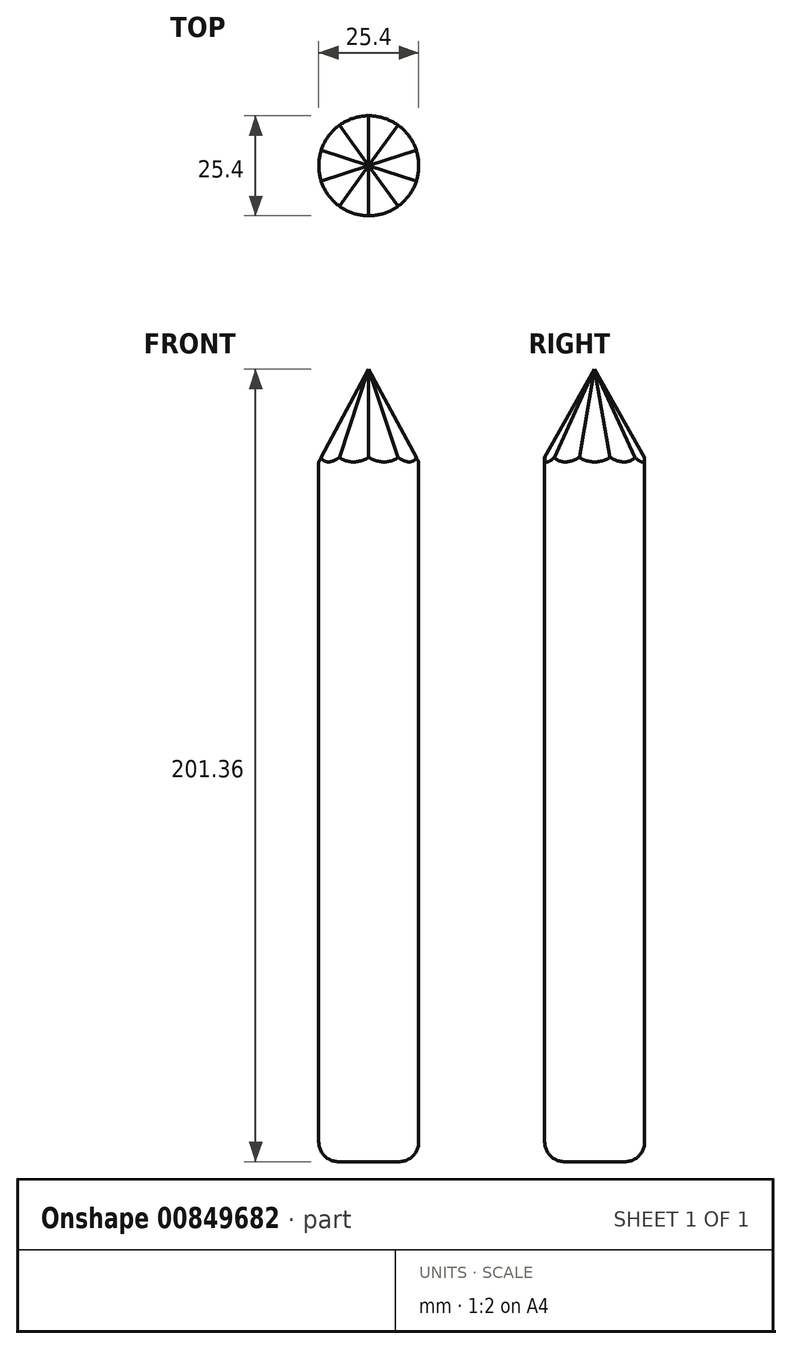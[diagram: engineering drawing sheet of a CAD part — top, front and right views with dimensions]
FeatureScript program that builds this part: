
annotation { "Feature Type Name" : "Feature", "Feature Type Description" : "" }
export const myFeature = defineFeature(function(context is Context, id is Id, definition is map)
    precondition{}
    {
        {
            var Q0;
            Q0=qCreatedBy(makeId("Top.planeOp"),FACE);
            var sketch = newSketch(context, id + "F0", { "sketchPlane" : qUnion([Q0])});
            skCircle(sketch, "E0.cCircle", {"center": v(0, 0) * mm, "radius": 12.7 * mm, "construction": true});
            skLineSegment(sketch, "E0.0", {"start": v(-12.7, -4.13) * mm, "end": v(-12.7, 4.13) * mm});
            skLineSegment(sketch, "E0.1", {"start": v(-12.7, 4.13) * mm, "end": v(-7.85, 10.8) * mm});
            skLineSegment(sketch, "E0.2", {"start": v(-7.85, 10.8) * mm, "end": v(0, 13.35) * mm});
            skLineSegment(sketch, "E0.3", {"start": v(0, 13.35) * mm, "end": v(7.85, 10.8) * mm});
            skLineSegment(sketch, "E0.4", {"start": v(7.85, 10.8) * mm, "end": v(12.7, 4.13) * mm});
            skLineSegment(sketch, "E0.5", {"start": v(12.7, 4.13) * mm, "end": v(12.7, -4.13) * mm});
            skLineSegment(sketch, "E0.6", {"start": v(12.7, -4.13) * mm, "end": v(7.85, -10.8) * mm});
            skLineSegment(sketch, "E0.7", {"start": v(7.85, -10.8) * mm, "end": v(0, -13.35) * mm});
            skLineSegment(sketch, "E0.8", {"start": v(0, -13.35) * mm, "end": v(-7.85, -10.8) * mm});
            skLineSegment(sketch, "E0.9", {"start": v(-7.85, -10.8) * mm, "end": v(-12.7, -4.13) * mm});
            skPoint(sketch, "E0.0.midPoint", {"position": v(-12.7, 0) * mm});
            skSolve(sketch);
        }
        {
            var Q0;
            Q0=qSketchRegion(id+"F0",true);
            extrude(context, id + "F1", {"entities" : qUnion([Q0]), "depth" : 177.8 * mm, "offsetDistance" : 25.4 * mm});
        }
        {
            var Q0;
            Q0=qCreatedBy(makeId("Front.planeOp"),FACE);
            var sketch = newSketch(context, id + "F2", { "sketchPlane" : qUnion([Q0])});
            skPoint(sketch, "E1", {"position": v(0, 201.36) * mm});
            skSolve(sketch);
        }
        {
            var Q1;
            Q1=makeQuery(id+"F1.opExtrude","CAP_FACE",FACE,{"disambiguationData":[OSD([sQuery(id+"F0.wireOp",EDGE,"E0.0"),sQuery(id+"F0.wireOp",EDGE,"E0.1"),sQuery(id+"F0.wireOp",EDGE,"E0.2"),sQuery(id+"F0.wireOp",EDGE,"E0.3"),sQuery(id+"F0.wireOp",EDGE,"E0.4"),sQuery(id+"F0.wireOp",EDGE,"E0.5"),sQuery(id+"F0.wireOp",EDGE,"E0.6"),sQuery(id+"F0.wireOp",EDGE,"E0.7"),sQuery(id+"F0.wireOp",EDGE,"E0.8"),sQuery(id+"F0.wireOp",EDGE,"E0.9")])],"isStart":false});
            var Q2;
            Q2=sQuery(id+"F2.wireOp",VERTEX,"E1");
            loft(context, id + "F3", {"operationType" : NewBodyOperationType.ADD, "sheetProfilesArray" : [{ "sheetProfileEntities" : qUnion([Q1]) }, { "sheetProfileEntities" : qUnion([Q2]) }]});
        }
        {
            var Q0;
            Q0=makeQuery(id+"F1.opExtrude","SWEPT_EDGE",EDGE,{"disambiguationData":[OSD([sQuery(id+"F0.wireOp",EDGE,"E0.7"),sQuery(id+"F0.wireOp",EDGE,"E0.8")])]});
            var Q1;
            Q1=makeQuery(id+"F1.opExtrude","SWEPT_EDGE",EDGE,{"disambiguationData":[OSD([sQuery(id+"F0.wireOp",EDGE,"E0.8"),sQuery(id+"F0.wireOp",EDGE,"E0.9")])]});
            var Q2;
            Q2=makeQuery(id+"F1.opExtrude","SWEPT_EDGE",EDGE,{"disambiguationData":[OSD([sQuery(id+"F0.wireOp",EDGE,"E0.0"),sQuery(id+"F0.wireOp",EDGE,"E0.9")])]});
            var Q3;
            Q3=makeQuery(id+"F1.opExtrude","SWEPT_EDGE",EDGE,{"disambiguationData":[OSD([sQuery(id+"F0.wireOp",EDGE,"E0.0"),sQuery(id+"F0.wireOp",EDGE,"E0.1")])]});
            var Q4;
            Q4=makeQuery(id+"F1.opExtrude","SWEPT_EDGE",EDGE,{"disambiguationData":[OSD([sQuery(id+"F0.wireOp",EDGE,"E0.1"),sQuery(id+"F0.wireOp",EDGE,"E0.2")])]});
            var Q5;
            Q5=makeQuery(id+"F1.opExtrude","SWEPT_EDGE",EDGE,{"disambiguationData":[OSD([sQuery(id+"F0.wireOp",EDGE,"E0.2"),sQuery(id+"F0.wireOp",EDGE,"E0.3")])]});
            var Q6;
            Q6=makeQuery(id+"F1.opExtrude","SWEPT_EDGE",EDGE,{"disambiguationData":[OSD([sQuery(id+"F0.wireOp",EDGE,"E0.3"),sQuery(id+"F0.wireOp",EDGE,"E0.4")])]});
            var Q7;
            Q7=makeQuery(id+"F1.opExtrude","SWEPT_EDGE",EDGE,{"disambiguationData":[OSD([sQuery(id+"F0.wireOp",EDGE,"E0.4"),sQuery(id+"F0.wireOp",EDGE,"E0.5")])]});
            var Q8;
            Q8=makeQuery(id+"F1.opExtrude","SWEPT_EDGE",EDGE,{"disambiguationData":[OSD([sQuery(id+"F0.wireOp",EDGE,"E0.5"),sQuery(id+"F0.wireOp",EDGE,"E0.6")])]});
            var Q9;
            Q9=makeQuery(id+"F1.opExtrude","SWEPT_EDGE",EDGE,{"disambiguationData":[OSD([sQuery(id+"F0.wireOp",EDGE,"E0.6"),sQuery(id+"F0.wireOp",EDGE,"E0.7")])]});
            fillet(context, id + "F4", {"entities" : qUnion([Q0, Q1, Q2, Q3, Q4, Q5, Q6, Q7, Q8, Q9]), "radius" : 12.7 * mm, "tangentPropagation" : true, "allowEdgeOverflow" : false});
        }
        {
            var Q0;
            {var subQ0=sQuery(id+"F0.wireOp",EDGE,"E0.9");var subQ1=sQuery(id+"F0.wireOp",EDGE,"E0.0");Q0=makeQuery(id+"F4.opFillet","BLEND_EDGE",EDGE,{"blendedFrom":[makeQuery(id+"F1.opExtrude","SWEPT_EDGE",EDGE,{"disambiguationData":[OSD([subQ1,subQ0])]}),makeQuery(id+"F1.opExtrude","CAP_FACE",FACE,{"disambiguationData":[OSD([subQ1,sQuery(id+"F0.wireOp",EDGE,"E0.1"),sQuery(id+"F0.wireOp",EDGE,"E0.2"),sQuery(id+"F0.wireOp",EDGE,"E0.3"),sQuery(id+"F0.wireOp",EDGE,"E0.4"),sQuery(id+"F0.wireOp",EDGE,"E0.5"),sQuery(id+"F0.wireOp",EDGE,"E0.6"),sQuery(id+"F0.wireOp",EDGE,"E0.7"),sQuery(id+"F0.wireOp",EDGE,"E0.8"),subQ0])],"isStart":true})],"blendedInto":[makeQuery(id+"F1.opExtrude","CAP_FACE",FACE,{"disambiguationData":[OSD([subQ1,sQuery(id+"F0.wireOp",EDGE,"E0.1"),sQuery(id+"F0.wireOp",EDGE,"E0.2"),sQuery(id+"F0.wireOp",EDGE,"E0.3"),sQuery(id+"F0.wireOp",EDGE,"E0.4"),sQuery(id+"F0.wireOp",EDGE,"E0.5"),sQuery(id+"F0.wireOp",EDGE,"E0.6"),sQuery(id+"F0.wireOp",EDGE,"E0.7"),sQuery(id+"F0.wireOp",EDGE,"E0.8"),subQ0])],"isStart":true})]});}
            fillet(context, id + "F5", {"entities" : qUnion([Q0]), "radius" : 5.08 * mm, "tangentPropagation" : true, "allowEdgeOverflow" : false});
        }
    });
